# Revit family: 2056342
name_source: partatom
category: Lighting Fixtures
revit_build: Autodesk Revit 2018 (Build: 20170223_1515(x64)
units: mm (PartAtom-declared; Revit-internal decimal feet)

## family parameters
Cut with Voids When Loaded = No
Host = Face
Light Source = Yes
OmniClass Number = 23.80.70.11.17
OmniClass Title = Specialized Lighting by Location or Use
Part Type = Normal
Room Calculation Point = No
Round Connector Dimension = Use Diameter
Shared = No

## types (1)
- 2056342 MYRIAD SQ HS FLOOD 4K DALI BLKRFL
    Accessory Length = 90 mm  [stored 0.295276 ft]
    Accessory Material = Aluminum_Sylvania_Myriad_White
    Accessory Type = Myriad Square - Accessories : Myriad Wh Bez Sq+Clear Glass
    Accessory Width = 90 mm  [stored 0.295276 ft]
    Apparent Load = 10 VA
    Assembly Code = D5020200
    Average life (h) - L70/B50 = 50000
    Beam Angle = 48°
    Body Material = Aluminum_Sylvania_Myriad_Gray
    Catalog Number = 2056314 MYRIDSQ HS FLD 4K STD
    Color Filter = 16777215
    Compatibile with bulbs of energy class = A++ A+ A
    Control gear availability = Yes
    Cutout Length = 73 mm  [stored 0.239501 ft]
    Cutout Width = 73 mm  [stored 0.239501 ft]
    Default Elevation = 0 mm  [stored 0 ft]
    Description = New high output high efficiency LED downlight modules IR/UV - free light source without heat radiation Energy efficient light source with far superior luminous flux per watt than existing Low Voltage Halogen Dimmable options including DALI as standard IP65 with Chrome bezel New range of Architectural accessories each providing a different lit dimension Colour temperatures warm 3000K Aluminium Reflector Luminaires supplied complete with LED drivers Emergency versions pass through cut out 25 degrees Total circuit power I5W
    Diffuser Material = Glass_Sylvania_Myriad_Clear_4000K
    Dimmable = No
    Dimming Lamp Color Temperature Shift = <None>
    Drive Current = 350mA
    Emit Shape Visible in Rendering = No
    Emit from Rectangle Length = 66 mm  [stored 0.216535 ft]
    Emit from Rectangle Width = 66 mm  [stored 0.216535 ft]
    Height = 64 mm  [stored 0.209974 ft]
    IK Rating = IK02
    IP Rating = IP20
    LOR = 1
    Length = 72 mm  [stored 0.23622 ft]
    Manufacturer = Feilo Sylvania
    Model = MYRIAD SQUARE HOUS FLOOD 4K DALI BLACK REFL
    Photometric Web File = 2056342.ies
    Product Family = MYRIAD SQUARE - FLOOD- HOUSING
    Product Page URL = http://www.feilosylvania.com
    Recessed depth = 64 mm  [stored 0.209974 ft]
    Reflector Material = Aluminum_Sylvania_Myriad_Bright
    Tilt Angle = -90°
    URL = 0
    Voltage = 230 V
    Voltage Comments = UNV (Universal Voltage; 220-240 Volt)
    Weight = 0 kg
    Width = 72 mm  [stored 0.23622 ft]

note: [stored X ft] marks values corroborated as IEEE doubles in the binary element streams (Revit-internal decimal feet)

## geometry (parser evidence)
native form markers: Sweep x5
no freeform markers — native parametric forms only
